# Revit family: Xtech_DécorSystems_CeilingRecess4
name_source: partatom
category: Generic Models
revit_build: Autodesk Revit 2014 (Build: 20140709_2115(x64)
units: mm (PartAtom-declared; Revit-internal decimal feet)

## types (1)
- Perimeos
    Assembly Code = E2010310
    AssetType = Fixed
    BIMObjectName = Xtech_DecorSystems_CeilingRecess_Perimeos
    Category = Pr_35_90_43_12:CeilingPerimeterTrims
    Color = RAL 9016 Satin
    Constituents = Ceiling Recess, with closure flap and interchangeable transition profiles
    Cost = 0 $
    Description = Perimeos Ceiling Recess for blinds and curtains
    DurationUnit = year
    ExpectedLife = 30
    Features = Locking closure flap, SpeedClip blind mounting brackets. Note the PT (Plain Transition) can be used for drylining, or alternatively on top of box to fit to wall. Note that the beam must be supported at 1 metre intervals with the suspension bracket, as detailed in specification PDF
    Finish = Polyester powder coated
    IfcExportAs = IfcFurnishingElement
    IfcExportType = DoorWindowShadingType
    ManufacturerName = DecorSystems
    ManufacturerURL = http://www.decorsystems.co.uk
    Material = Aluminium 6063 Alloy T6
    ModelNumber = PRM01
    NBSDescription = GeneralFittings,FurnishingsAndEquipmentSystem
    NBSReference = 45-75-95/405
    Name = CeilingRecess_Perimeos_DecorSystems
    NominalHeight = 100 mm  [stored 0.328084 ft]
    NominalLength = 0 mm  [stored 0 ft]
    NominalWidth = 130 mm  [stored 0.426509 ft]
    ProductInformation = http://www.decorsystems.co.uk
    Shape = Inverted U channel
    URL = http://www.decorsystems.co.uk
    Uniclass2 = Pr_35_90_43_12
    Version = 1
    WarrantyDescription = http://www.decorsystems.co.uk
    WarrantyDurationLabor = 3
    WarrantyDurationParts = 5
    WarrantyDurationUnit = year

note: [stored X ft] marks values corroborated as IEEE doubles in the binary element streams (Revit-internal decimal feet)

## geometry (parser evidence)
native form markers: Blend x2, Sweep x37
no freeform markers — native parametric forms only
